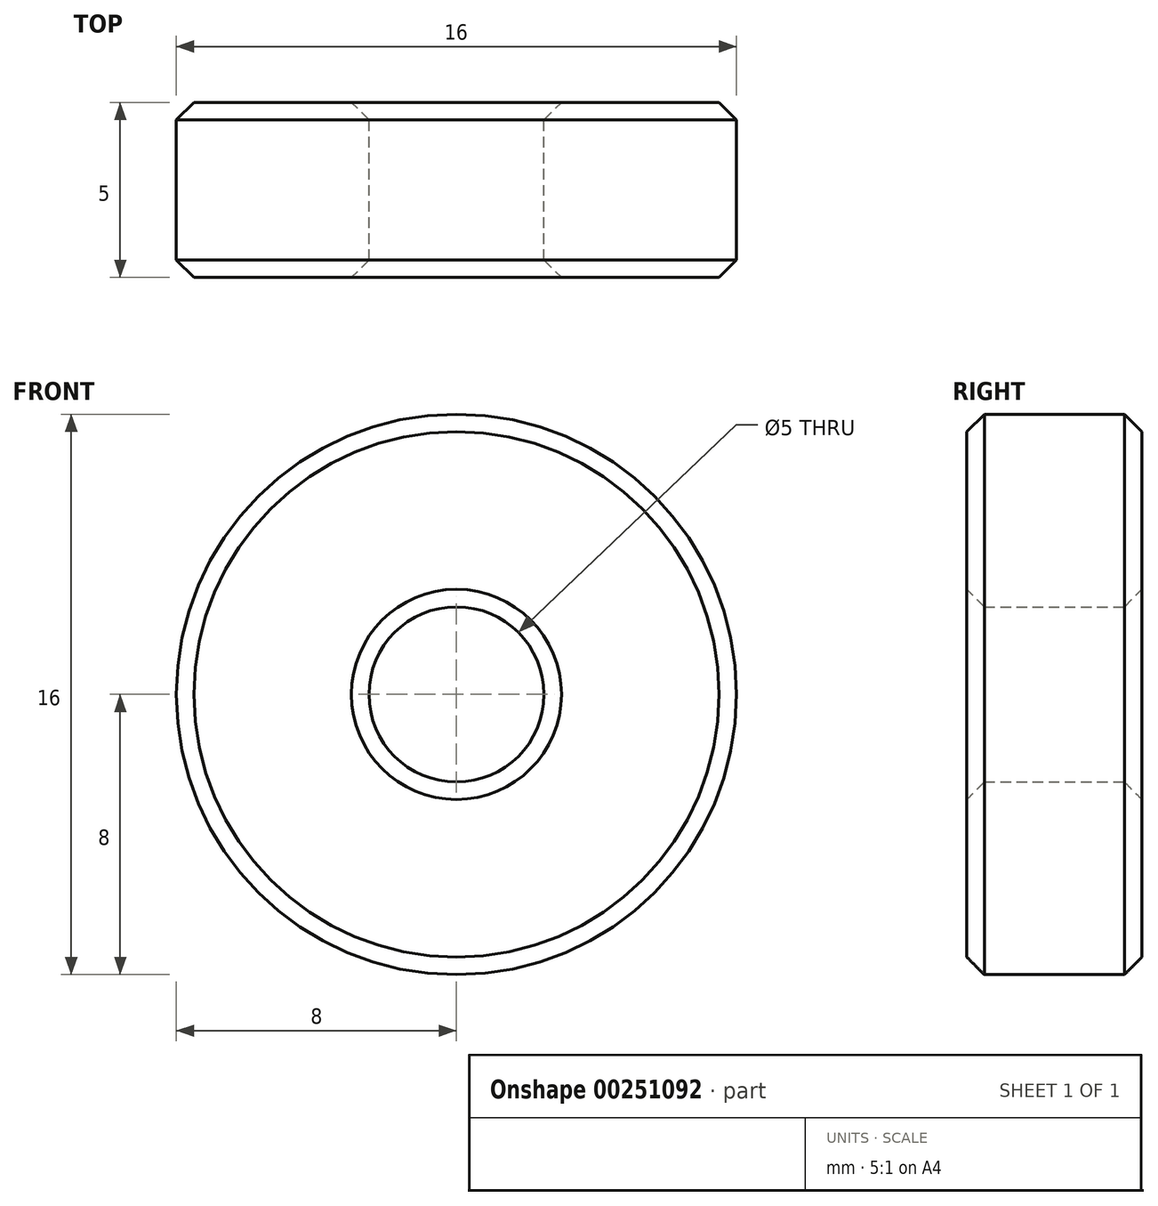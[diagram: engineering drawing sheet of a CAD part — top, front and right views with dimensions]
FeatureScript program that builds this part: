
annotation { "Feature Type Name" : "Feature", "Feature Type Description" : "" }
export const myFeature = defineFeature(function(context is Context, id is Id, definition is map)
    precondition{}
    {
        {
            var Q0;
            Q0=qCreatedBy(makeId("Front.planeOp"),FACE);
            var sketch = newSketch(context, id + "F0", { "sketchPlane" : qUnion([Q0])});
            skCircle(sketch, "E0", {"center": v(0, 0) * mm, "radius": 8 * mm});
            skCircle(sketch, "E1", {"center": v(0, 0) * mm, "radius": 2.5 * mm});
            skSolve(sketch);
        }
        {
            var Q0;
            Q0 = qSketchRegion(id + "F0", true);
            extrude(context, id + "F1", {"entities" : qUnion([Q0]), "depth" : 5 * mm});
        }
        {
            var Q0;
            Q0=makeQuery(id+"F1.opExtrude","CAP_EDGE",EDGE,{"disambiguationData":[OSD([sQuery(id+"F0.wireOp",EDGE,"E0")])],"isStart":false});
            var Q1;
            Q1=makeQuery(id+"F1.opExtrude","CAP_EDGE",EDGE,{"disambiguationData":[OSD([sQuery(id+"F0.wireOp",EDGE,"E0")])],"isStart":true});
            var Q2;
            Q2=makeQuery(id+"F1.opExtrude","CAP_EDGE",EDGE,{"disambiguationData":[OSD([sQuery(id+"F0.wireOp",EDGE,"E1")])],"isStart":true});
            var Q3;
            Q3=makeQuery(id+"F1.opExtrude","CAP_EDGE",EDGE,{"disambiguationData":[OSD([sQuery(id+"F0.wireOp",EDGE,"E1")])],"isStart":false});
            chamfer(context, id + "F2", {"entities" : qUnion([Q0, Q1, Q2, Q3]), "width" : .5 * mm, "tangentPropagation" : true});
        }
    });
